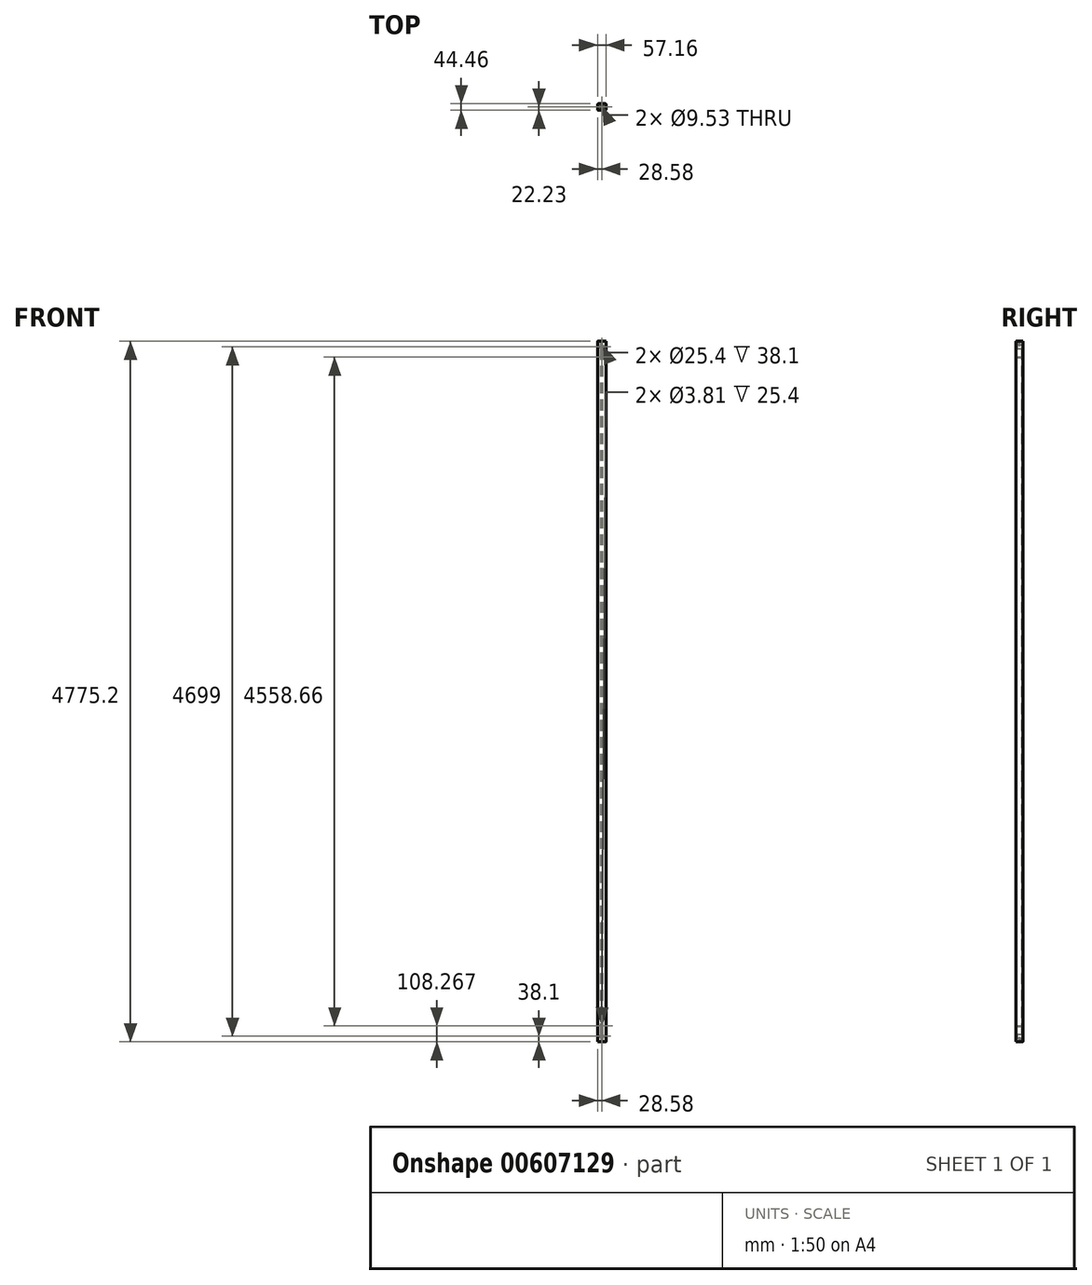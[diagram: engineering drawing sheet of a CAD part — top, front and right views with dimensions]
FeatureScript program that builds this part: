
annotation { "Feature Type Name" : "Feature", "Feature Type Description" : "" }
export const myFeature = defineFeature(function(context is Context, id is Id, definition is map)
    precondition{}
    {
        {
            var Q0;
            Q0=qCreatedBy(makeId("Top.planeOp"),FACE);
            var sketch = newSketch(context, id + "F0", { "sketchPlane" : qUnion([Q0])});
            skLineSegment(sketch, "E0.bottom", {"start": v(22.22, -22.22) * mm, "end": v(-22.23, -22.23) * mm});
            skLineSegment(sketch, "E0.top", {"start": v(22.23, 22.23) * mm, "end": v(-22.23, 22.22) * mm});
            skLineSegment(sketch, "E0.left", {"start": v(28.57, -15.87) * mm, "end": v(28.57, 15.88) * mm});
            skLineSegment(sketch, "E0.right", {"start": v(-28.58, -15.88) * mm, "end": v(-28.58, 15.87) * mm});
            skPoint(sketch, "E0.middle", {"position": v(0, 0) * mm});
            skPoint(sketch, "E1.visualSharp", {"position": v(-28.58, 22.22) * mm});
            skArc(sketch, "E1.filletArc", {"start": v(-22.23, 22.23) * mm, "mid": v(-26.72, 20.37) * mm, "end": v(-28.58, 15.87) * mm});
            skPoint(sketch, "E2.visualSharp", {"position": v(28.58, 22.23) * mm});
            skArc(sketch, "E2.filletArc", {"start": v(28.58, 15.88) * mm, "mid": v(26.72, 20.37) * mm, "end": v(22.23, 22.23) * mm});
            skPoint(sketch, "E3.visualSharp", {"position": v(28.57, -22.22) * mm});
            skArc(sketch, "E3.filletArc", {"start": v(22.22, -22.23) * mm, "mid": v(26.72, -20.37) * mm, "end": v(28.57, -15.87) * mm});
            skPoint(sketch, "E4.visualSharp", {"position": v(-28.58, -22.23) * mm});
            skArc(sketch, "E4.filletArc", {"start": v(-28.58, -15.88) * mm, "mid": v(-26.72, -20.37) * mm, "end": v(-22.23, -22.23) * mm});
            skSolve(sketch);
        }
        {
            var Q0;
            Q0 = qSketchRegion(id + "F0", true);
            extrude(context, id + "F1", {"entities" : qUnion([Q0]), "depth" : 4775.2 * mm, "offsetDistance" : 25.4 * mm});
        }
        {
            var Q0;
            Q0=makeQuery(id+"F1.opExtrude","SWEPT_FACE",FACE,{"disambiguationData":[OSD([sQuery(id+"F0.wireOp",EDGE,"E0.top")])]});
            var sketch = newSketch(context, id + "F2", { "sketchPlane" : qUnion([Q0])});
            skPoint(sketch, "E5.centerSnap0", {"position": v(0, 4775.2) * mm});
            skCircle(sketch, "E6", {"center": v(0, 38.1) * mm, "radius": 12.7 * mm});
            skCircle(sketch, "E7", {"center": v(0, 4737.1) * mm, "radius": 12.7 * mm});
            skSolve(sketch);
        }
        {
            var Q0;
            Q0 = qSketchRegion(id + "F2", true);
            var Q1;
            Q1 = qConstructionFilter(qBodyType(qCreatedBy(id + "F2" ,EDGE), BodyType.WIRE), ConstructionObject.NO);
            extrude(context, id + "F3", {"entities" : qUnion([Q0]), "operationType" : NewBodyOperationType.REMOVE, "surfaceEntities" : qUnion([Q1]), "oppositeDirection" : true, "depth" : 38.1 * mm, "offsetDistance" : 25.4 * mm});
        }
        {
            var Q0;
            Q0=makeQuery(id+"F1.opExtrude","SWEPT_FACE",FACE,{"disambiguationData":[OSD([sQuery(id+"F0.wireOp",EDGE,"E0.top")])]});
            var sketch = newSketch(context, id + "F4", { "sketchPlane" : qUnion([Q0])});
            skLineSegment(sketch, "E8.bottom", {"start": v(-6.35, 38.1) * mm, "end": v(6.35, 38.1) * mm});
            skLineSegment(sketch, "E8.top", {"start": v(-6.35, 4737.1) * mm, "end": v(6.35, 4737.1) * mm});
            skLineSegment(sketch, "E8.left", {"start": v(-6.35, 38.1) * mm, "end": v(-6.35, 4737.1) * mm});
            skLineSegment(sketch, "E8.right", {"start": v(6.35, 38.1) * mm, "end": v(6.35, 4737.1) * mm});
            skSolve(sketch);
        }
        {
            var Q0;
            Q0 = qSketchRegion(id + "F4", true);
            extrude(context, id + "F5", {"entities" : qUnion([Q0]), "operationType" : NewBodyOperationType.REMOVE, "oppositeDirection" : true, "depth" : 6.35 * mm, "offsetDistance" : 25.4 * mm});
        }
        {
            var Q0;
            Q0=makeQuery(id+"F1.opExtrude","CAP_FACE",FACE,{"disambiguationData":[OSD([sQuery(id+"F0.wireOp",EDGE,"E0.bottom"),sQuery(id+"F0.wireOp",EDGE,"E0.top"),sQuery(id+"F0.wireOp",EDGE,"E0.left"),sQuery(id+"F0.wireOp",EDGE,"E0.right"),sQuery(id+"F0.wireOp",EDGE,"E1.filletArc"),sQuery(id+"F0.wireOp",EDGE,"E2.filletArc"),sQuery(id+"F0.wireOp",EDGE,"E3.filletArc"),sQuery(id+"F0.wireOp",EDGE,"E4.filletArc")])],"isStart":false});
            var sketch = newSketch(context, id + "F6", { "sketchPlane" : qUnion([Q0])});
            skCircle(sketch, "E9", {"center": v(0, 0) * mm, "radius": 4.76 * mm});
            skSolve(sketch);
        }
        {
            var Q0;
            Q0 = qSketchRegion(id + "F6", true);
            extrude(context, id + "F7", {"entities" : qUnion([Q0]), "operationType" : NewBodyOperationType.REMOVE, "oppositeDirection" : true, "depth" : 38.1 * mm, "offsetDistance" : 25.4 * mm});
        }
        {
            var Q0;
            Q0=makeQuery(id+"F1.opExtrude","CAP_FACE",FACE,{"disambiguationData":[OSD([sQuery(id+"F0.wireOp",EDGE,"E0.bottom"),sQuery(id+"F0.wireOp",EDGE,"E0.top"),sQuery(id+"F0.wireOp",EDGE,"E0.left"),sQuery(id+"F0.wireOp",EDGE,"E0.right"),sQuery(id+"F0.wireOp",EDGE,"E1.filletArc"),sQuery(id+"F0.wireOp",EDGE,"E2.filletArc"),sQuery(id+"F0.wireOp",EDGE,"E3.filletArc"),sQuery(id+"F0.wireOp",EDGE,"E4.filletArc")])],"isStart":true});
            var sketch = newSketch(context, id + "F8", { "sketchPlane" : qUnion([Q0])});
            skCircle(sketch, "E10", {"center": v(0, 0) * mm, "radius": 4.76 * mm});
            skSolve(sketch);
        }
        {
            var Q0;
            Q0 = qSketchRegion(id + "F8", true);
            extrude(context, id + "F9", {"entities" : qUnion([Q0]), "operationType" : NewBodyOperationType.REMOVE, "oppositeDirection" : true, "depth" : 38.1 * mm, "offsetDistance" : 25.4 * mm});
        }
        {
            var Q0;
            Q0=makeQuery(id+"F5.boolean.opBoolean","COPY",FACE,{"derivedFrom":makeQuery(id+"F5.opExtrude","CAP_FACE",FACE,{"disambiguationData":[OSD([sQuery(id+"F4.wireOp",EDGE,"E8.bottom"),sQuery(id+"F4.wireOp",EDGE,"E8.top"),sQuery(id+"F4.wireOp",EDGE,"E8.left"),sQuery(id+"F4.wireOp",EDGE,"E8.right")])],"isStart":false})});
            var sketch = newSketch(context, id + "F10", { "sketchPlane" : qUnion([Q0])});
            skCircle(sketch, "E11", {"center": v(0, 4666.93) * mm, "radius": 1.9 * mm});
            skCircle(sketch, "E12", {"center": v(0, 108.27) * mm, "radius": 1.9 * mm});
            skSolve(sketch);
        }
        {
            var Q0;
            Q0 = qSketchRegion(id + "F10", true);
            extrude(context, id + "F11", {"entities" : qUnion([Q0]), "operationType" : NewBodyOperationType.REMOVE, "oppositeDirection" : true, "depth" : 25.4 * mm, "offsetDistance" : 25.4 * mm});
        }
    });
